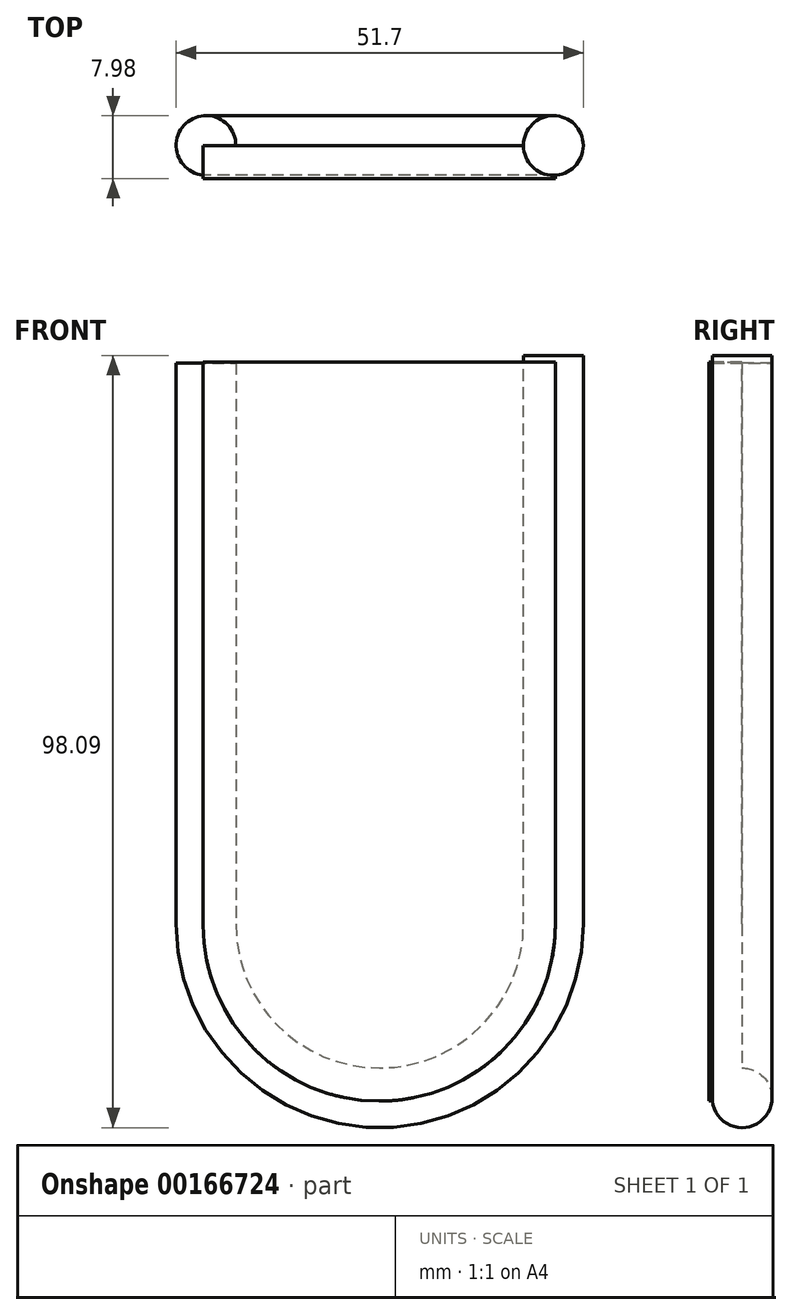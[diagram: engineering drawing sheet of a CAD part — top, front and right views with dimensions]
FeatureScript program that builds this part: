
annotation { "Feature Type Name" : "Feature", "Feature Type Description" : "" }
export const myFeature = defineFeature(function(context is Context, id is Id, definition is map)
    precondition{}
    {
        {
            var Q0;
            Q0=qCreatedBy(makeId("Front.planeOp"),FACE);
            var sketch = newSketch(context, id + "F0", { "sketchPlane" : qUnion([Q0])});
            skLineSegment(sketch, "E0", {"start": v(-44.6, 57.57) * mm, "end": v(-44.6, -13.74) * mm});
            skArc(sketch, "E1", {"start": v(-44.6, -13.74) * mm, "mid": v(-22.3, -36.04) * mm, "end": v(0, -13.74) * mm});
            skLineSegment(sketch, "E2", {"start": v(0, -13.74) * mm, "end": v(0, 58.5) * mm});
            skSolve(sketch);
        }
        {
            var Q0;
            Q0=sQuery(id+"F0.wireOp",VERTEX,"E0.start");
            var Q1;
            Q1=sQuery(id+"F0.wireOp",EDGE,"E0");
            cPlane(context, id + "F1", {"entities" : qUnion([Q0, Q1]), "cplaneType" : CPlaneType.CURVE_POINT, "offset" : 25.4 * mm, "width" : 152.4 * mm, "height" : 152.4 * mm});
        }
        {
            var Q0;
            Q0=qCreatedBy(id+"F1.planeOp",FACE);
            var sketch = newSketch(context, id + "F2", { "sketchPlane" : qUnion([Q0])});
            skCircle(sketch, "E3", {"center": v(-44.36, 0) * mm, "radius": 3.8 * mm});
            skSolve(sketch);
        }
        {
            var Q0;
            Q0=makeQuery(id+"F2.imprint","IMPRINT",FACE,{"disambiguationData":[TD([[makeQuery(id+"F2.imprint","IMPRINT",EDGE,{"derivedFrom":sQuery(id+"F2.wireOp",EDGE,"E3")}),1.0]])]});
            var Q1;
            Q1=sQuery(id+"F0.wireOp",EDGE,"E0");
            var Q2;
            Q2=sQuery(id+"F0.wireOp",EDGE,"E1");
            var Q3;
            Q3=sQuery(id+"F0.wireOp",EDGE,"E2");
            sweep(context, id + "F3", {"profiles" : qUnion([Q0]), "path" : qUnion([Q1, Q2, Q3])});
        }
        {
            var Q0;
            Q0=qCreatedBy(makeId("Front.planeOp"),FACE);
            var sketch = newSketch(context, id + "F4", { "sketchPlane" : qUnion([Q0])});
            skLineSegment(sketch, "E4.bottom", {"start": v(-44.72, 57.7) * mm, "end": v(0, 57.7) * mm});
            skLineSegment(sketch, "E4.top", {"start": v(-44.72, -13.85) * mm, "end": v(0, -13.85) * mm});
            skLineSegment(sketch, "E4.left", {"start": v(-44.72, 57.7) * mm, "end": v(-44.72, -13.85) * mm});
            skLineSegment(sketch, "E4.right", {"start": v(0, 57.7) * mm, "end": v(0, -13.85) * mm});
            skArc(sketch, "E5", {"start": v(-44.72, -13.85) * mm, "mid": v(-22.36, -36.21) * mm, "end": v(0, -13.85) * mm});
            skSolve(sketch);
        }
        {
            var Q0;
            Q0=makeQuery(id+"F4.imprint","IMPRINT",FACE,{"disambiguationData":[TD([[makeQuery(id+"F4.imprint","IMPRINT",EDGE,{"derivedFrom":sQuery(id+"F4.wireOp",EDGE,"E4.bottom")}),-1.0]])]});
            var Q1;
            Q1=makeQuery(id+"F4.imprint","IMPRINT",FACE,{"disambiguationData":[TD([[makeQuery(id+"F4.imprint","IMPRINT",EDGE,{"derivedFrom":sQuery(id+"F4.wireOp",EDGE,"E4.top")}),-1.0]])]});
            extrude(context, id + "F5", {"entities" : qUnion([Q0, Q1]), "operationType" : NewBodyOperationType.ADD, "depth" : 1.27 * mm});
        }
        {
            var Q0;
            Q0=makeQuery(id+"F4.imprint","IMPRINT",FACE,{"disambiguationData":[TD([[makeQuery(id+"F4.imprint","IMPRINT",EDGE,{"derivedFrom":sQuery(id+"F4.wireOp",EDGE,"E4.bottom")}),-1.0]])]});
            var Q1;
            Q1=makeQuery(id+"F4.imprint","IMPRINT",FACE,{"disambiguationData":[TD([[makeQuery(id+"F4.imprint","IMPRINT",EDGE,{"derivedFrom":sQuery(id+"F4.wireOp",EDGE,"E4.top")}),-1.0]])]});
            extrude(context, id + "F6", {"entities" : qUnion([Q0, Q1]), "operationType" : NewBodyOperationType.ADD, "depth" : 4.2 * mm});
        }
    });
